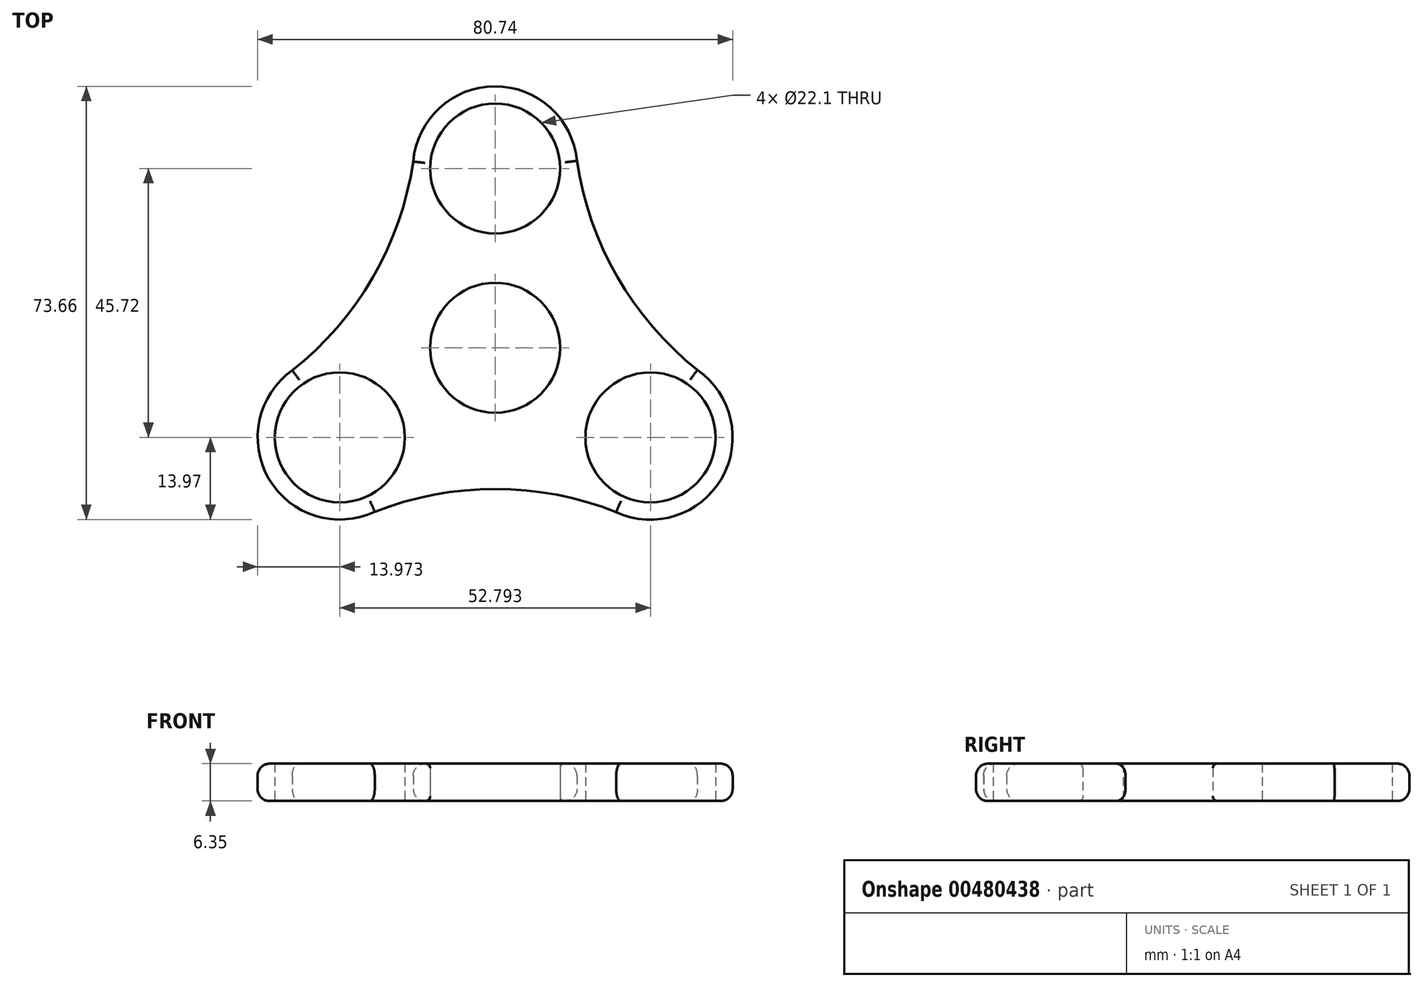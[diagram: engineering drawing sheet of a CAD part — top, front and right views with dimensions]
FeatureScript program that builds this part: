
annotation { "Feature Type Name" : "Feature", "Feature Type Description" : "" }
export const myFeature = defineFeature(function(context is Context, id is Id, definition is map)
    precondition{}
    {
        {
            var Q0;
            Q0=qCreatedBy(makeId("Top.planeOp"),FACE);
            var sketch = newSketch(context, id + "F0", { "sketchPlane" : qUnion([Q0])});
            skCircle(sketch, "E0", {"center": v(0, 0) * mm, "radius": 44.45 * mm});
            skCircle(sketch, "E1", {"center": v(0, 0) * mm, "radius": 11.05 * mm});
            skCircle(sketch, "E2", {"center": v(0, 30.48) * mm, "radius": 11.05 * mm});
            skCircle(sketch, "E3.1.0", {"center": v(-26.4, -15.24) * mm, "radius": 11.05 * mm});
            skCircle(sketch, "E3.2.0", {"center": v(26.4, -15.24) * mm, "radius": 11.05 * mm});
            skCircle(sketch, "E4", {"center": v(0, 30.48) * mm, "radius": 13.97 * mm});
            skCircle(sketch, "E5", {"center": v(-26.4, -15.24) * mm, "radius": 13.97 * mm});
            skCircle(sketch, "E6", {"center": v(26.4, -15.24) * mm, "radius": 13.97 * mm});
            skCircle(sketch, "E7", {"center": v(0, 0) * mm, "radius": 13.97 * mm});
            skArc(sketch, "E8", {"start": v(13.9, 31.78) * mm, "mid": v(20.76, 12.05) * mm, "end": v(34.38, -3.78) * mm});
            skArc(sketch, "E9.1.0", {"start": v(-34.48, -3.85) * mm, "mid": v(-20.82, 11.95) * mm, "end": v(-13.92, 31.67) * mm});
            skArc(sketch, "E9.2.0", {"start": v(20.57, -27.94) * mm, "mid": v(0.06, -24) * mm, "end": v(-20.46, -27.89) * mm});
            skSolve(sketch);
        }
        {
            var Q0;
            Q0=makeQuery(id+"F0.imprint","IMPRINT",FACE,{"disambiguationData":[TD([[makeQuery(id+"F0.imprint","IMPRINT",EDGE,{"derivedFrom":sQuery(id+"F0.wireOp",EDGE,"E2")}),-1.0]])]});
            var Q1;
            Q1=makeQuery(id+"F0.imprint","IMPRINT",FACE,{"disambiguationData":[TD([[makeQuery(id+"F0.imprint","IMPRINT",EDGE,{"derivedFrom":sQuery(id+"F0.wireOp",EDGE,"E3.2.0")}),-1.0]])]});
            var Q2;
            Q2=makeQuery(id+"F0.imprint","IMPRINT",FACE,{"disambiguationData":[TD([[makeQuery(id+"F0.imprint","IMPRINT",EDGE,{"derivedFrom":sQuery(id+"F0.wireOp",EDGE,"E3.1.0")}),-1.0]])]});
            var Q3;
            Q3=makeQuery(id+"F0.imprint","IMPRINT",FACE,{"disambiguationData":[TD([[makeQuery(id+"F0.imprint","IMPRINT",EDGE,{"derivedFrom":sQuery(id+"F0.wireOp",EDGE,"E7")}),-1.0]])]});
            var Q4;
            Q4=makeQuery(id+"F0.imprint","IMPRINT",FACE,{"disambiguationData":[TD([[makeQuery(id+"F0.imprint","IMPRINT",EDGE,{"derivedFrom":sQuery(id+"F0.wireOp",EDGE,"E1")}),-1.0]])]});
            extrude(context, id + "F1", {"entities" : qUnion([Q0, Q1, Q2, Q3, Q4]), "depth" : 6.35 * mm});
        }
        {
            var Q0;
            Q0=makeQuery(id+"F1.opExtrude","CAP_EDGE",EDGE,{"disambiguationData":[OSD([sQuery(id+"F0.wireOp",EDGE,"E6")])],"isStart":false});
            var Q1;
            Q1=makeQuery(id+"F1.opExtrude","CAP_EDGE",EDGE,{"disambiguationData":[OSD([sQuery(id+"F0.wireOp",EDGE,"E6")])],"isStart":true});
            var Q2;
            Q2=makeQuery(id+"F1.opExtrude","CAP_EDGE",EDGE,{"disambiguationData":[OSD([sQuery(id+"F0.wireOp",EDGE,"E5")])],"isStart":false});
            var Q3;
            Q3=makeQuery(id+"F1.opExtrude","CAP_EDGE",EDGE,{"disambiguationData":[OSD([sQuery(id+"F0.wireOp",EDGE,"E4")])],"isStart":false});
            var Q4;
            Q4=makeQuery(id+"F1.opExtrude","CAP_EDGE",EDGE,{"disambiguationData":[OSD([sQuery(id+"F0.wireOp",EDGE,"E5")])],"isStart":true});
            var Q5;
            Q5=makeQuery(id+"F1.opExtrude","CAP_EDGE",EDGE,{"disambiguationData":[OSD([sQuery(id+"F0.wireOp",EDGE,"E4")])],"isStart":true});
            fillet(context, id + "F2", {"entities" : qUnion([Q0, Q1, Q2, Q3, Q4, Q5]), "radius" : 2.03 * mm, "tangentPropagation" : true, "allowEdgeOverflow" : false});
        }
        {
            var Q0;
            Q0=makeQuery(id+"F1.opExtrude","CAP_EDGE",EDGE,{"disambiguationData":[OSD([sQuery(id+"F0.wireOp",EDGE,"E1")])],"isStart":false});
            var Q1;
            Q1=makeQuery(id+"F1.opExtrude","CAP_EDGE",EDGE,{"disambiguationData":[OSD([sQuery(id+"F0.wireOp",EDGE,"E1")])],"isStart":true});
            fillet(context, id + "F3", {"entities" : qUnion([Q0, Q1]), "radius" : 0.76 * mm, "tangentPropagation" : true, "allowEdgeOverflow" : false});
        }
    });
